# Revit family: 6dc57736_928d_4f3a_83f5_7543a74c3772
name_source: partatom
category: Generic Models
revit_build: Autodesk Revit Architecture 2015 (Build: 20140606_1530(x64)
units: mm (PartAtom-declared; Revit-internal decimal feet)

## types (1)
- Default
    BIMobject category = Basins
    BOSUseNativeGeometries = 0
    Brand url = http://www.duravit.com
    Date of publishing = 1/11/2017
    Edition number = 1
    IFC Classification = Sanitary Terminal
    Installation instructions = http://pro.duravit.com
    Manufacturer name = DURAVIT
    Masterformat 2014 Code = 33 81 29
    Masterformat 2014 Description = Communications Vaults, Pedestals, and Enclosures
    NBS Reference Code = 35-65-70-75
    NBS Reference Description = Sanitary Accessory Systems
    Nominal height = 0
    Nominal width = 210
    OmniClass Code = 23-21 25 23 15
    OmniClass Description = Pedestals
    Product Guid = 4909a972-e579-461c-bf50-6cb430ed3be7
    Product SKU = me-by-starck-pedestal-085839
    Product certification = http://pro.duravit.com
    Product data url = https://bimobject.com
    Product family = ME by Starck
    Product group = Pedestal
    Product name = ME by Starck Pedestal 085839
    Product url = http://pro.duravit.com
    QR code = http://bimobject.com
    Technical description = http://pro.duravit.com
    UNSPSC Code = 301815
    Uniclass 1.4 Code = L721
    Uniclass 1.4 Description = Sanitary equipment
    Uniclass 2.0 Code = SS-35-65-70-75
    Uniclass 2.0 Description = Sanitary Accessory Systems
    Uniclass 2015 Code = Pr_20_85_47
    Uniclass 2015 Name = Legs, pedestals, hangers and stringers
    Uniformat II Code = D2010
    Uniformat II Description = Plumbing Fixtures
    Weight Net (Kg) = 15.4

## geometry (parser evidence)
native form markers: Sweep x3
no freeform markers — native parametric forms only
